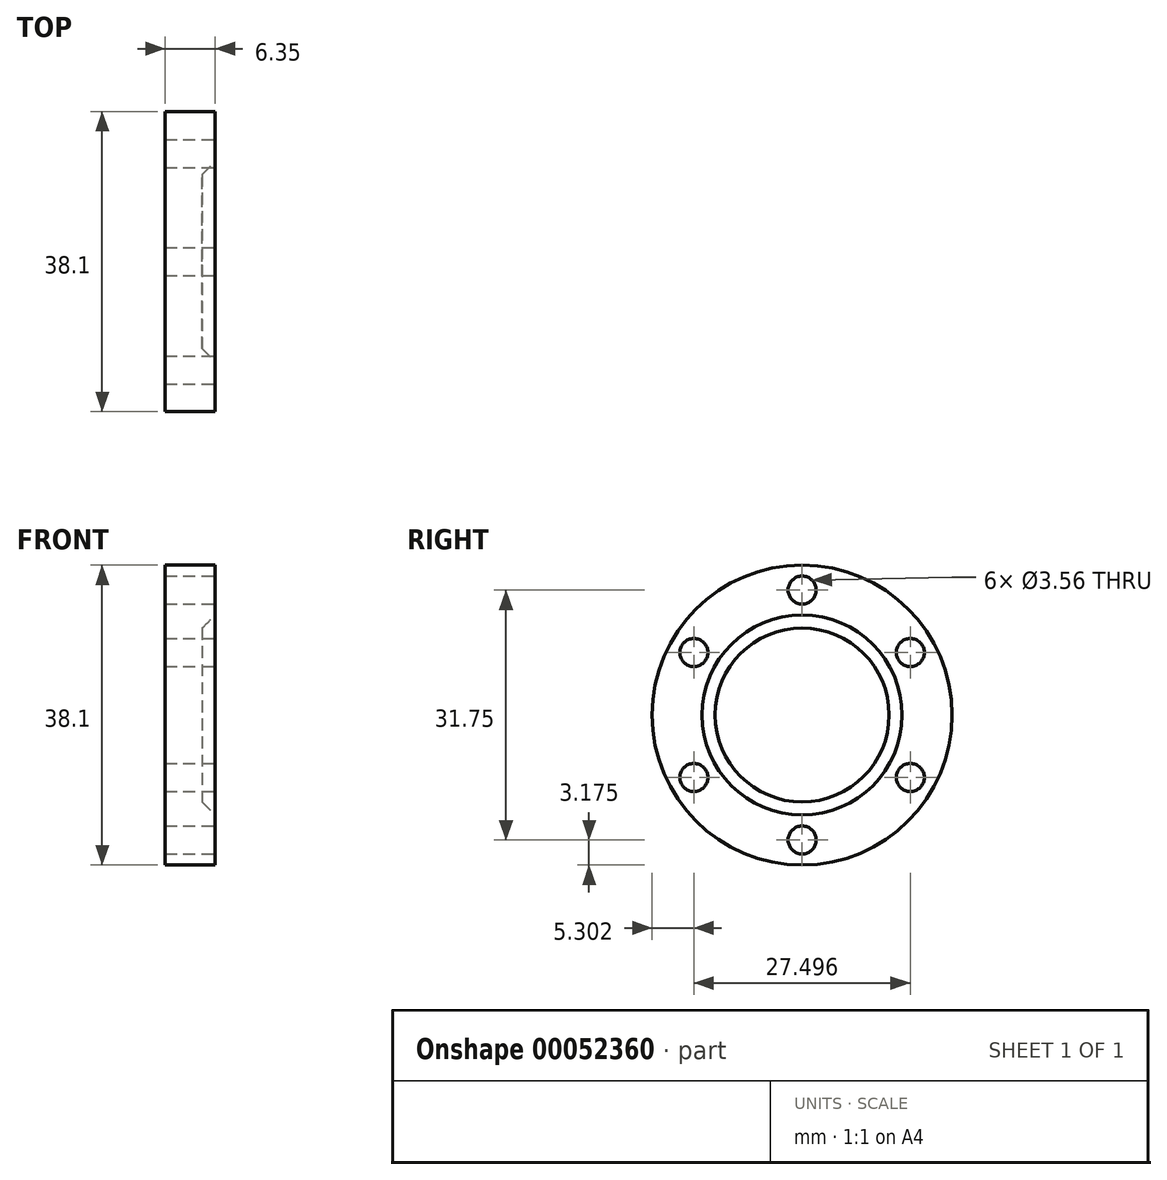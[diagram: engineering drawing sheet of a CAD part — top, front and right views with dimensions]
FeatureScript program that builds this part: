
annotation { "Feature Type Name" : "Feature", "Feature Type Description" : "" }
export const myFeature = defineFeature(function(context is Context, id is Id, definition is map)
    precondition{}
    {
        {
            var Q0;
            Q0=qCreatedBy(makeId("Front.planeOp"),FACE);
            var sketch = newSketch(context, id + "F0", { "sketchPlane" : qUnion([Q0])});
            skLineSegment(sketch, "E0", {"start": v(0, 12.7) * mm, "end": v(0, 19.05) * mm});
            skLineSegment(sketch, "E1", {"start": v(0, 19.05) * mm, "end": v(-6.35, 19.05) * mm});
            skLineSegment(sketch, "E2", {"start": v(-6.35, 19.05) * mm, "end": v(-6.35, 0) * mm});
            skLineSegment(sketch, "E3", {"start": v(-1.65, 11.05) * mm, "end": v(0, 12.7) * mm});
            skLineSegment(sketch, "E4", {"start": v(-6.35, 0) * mm, "end": v(-1.65, 0) * mm});
            skLineSegment(sketch, "E5", {"start": v(-1.65, 0) * mm, "end": v(-1.65, 11.05) * mm});
            skSolve(sketch);
        }
        {
            var Q0;
            Q0 = qSketchRegion(id + "F0", true);
            var Q1;
            Q1=sQuery(id+"F0.wireOp",EDGE,"E4");
            revolve(context, id + "F1", {"entities" : qUnion([Q0]), "axis" : qUnion([Q1]), "revolveType" : RevolveType.FULL});
        }
        {
            var Q0;
            Q0=qCreatedBy(makeId("Right.planeOp"),FACE);
            var sketch = newSketch(context, id + "F2", { "sketchPlane" : qUnion([Q0])});
            skCircle(sketch, "E6", {"center": v(0, 15.88) * mm, "radius": 1.78 * mm});
            skCircle(sketch, "E7", {"center": v(0, 0) * mm, "radius": 15.88 * mm, "construction": true});
            skCircle(sketch, "E8.1.0", {"center": v(-13.75, 7.94) * mm, "radius": 1.78 * mm});
            skCircle(sketch, "E8.2.0", {"center": v(-13.75, -7.94) * mm, "radius": 1.78 * mm});
            skCircle(sketch, "E8.3.0", {"center": v(0, -15.88) * mm, "radius": 1.78 * mm});
            skCircle(sketch, "E8.4.0", {"center": v(13.75, -7.94) * mm, "radius": 1.78 * mm});
            skCircle(sketch, "E8.5.0", {"center": v(13.75, 7.94) * mm, "radius": 1.78 * mm});
            skSolve(sketch);
        }
        {
            var Q0;
            Q0 = qSketchRegion(id + "F2", true);
            extrude(context, id + "F3", {"entities" : qUnion([Q0]), "operationType" : NewBodyOperationType.REMOVE, "endBound" : BoundingType.THROUGH_ALL, "oppositeDirection" : true, "depth" : 25.4 * mm});
        }
    });
